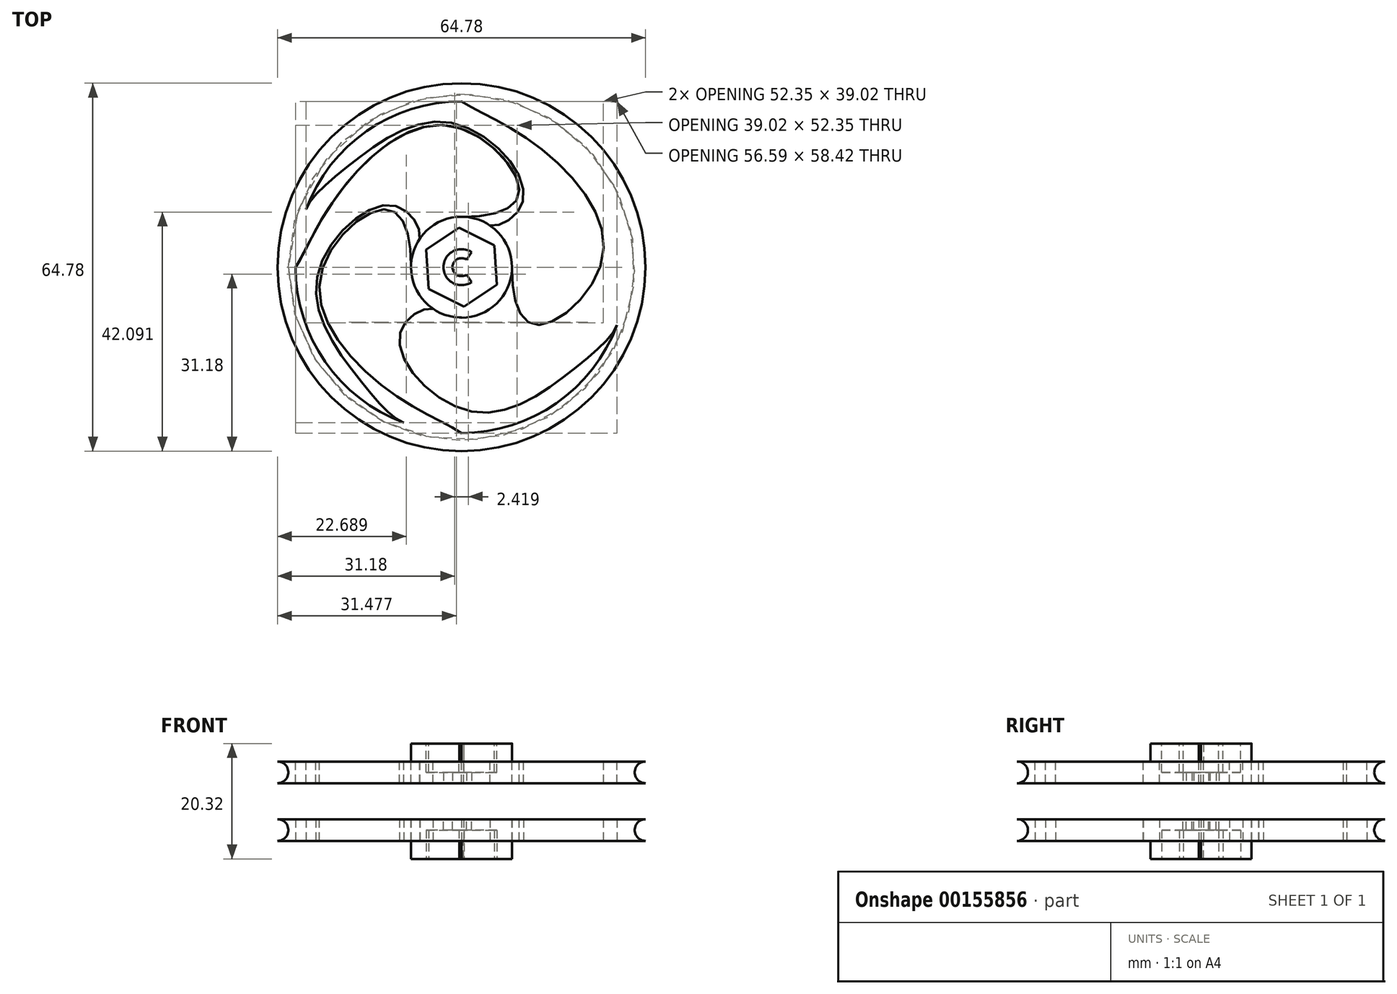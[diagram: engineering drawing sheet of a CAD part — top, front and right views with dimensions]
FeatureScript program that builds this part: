
annotation { "Feature Type Name" : "Feature", "Feature Type Description" : "" }
export const myFeature = defineFeature(function(context is Context, id is Id, definition is map)
    precondition{}
    {
        {
            var Q0;
            Q0=qCreatedBy(makeId("Front.planeOp"),FACE);
            var sketch = newSketch(context, id + "F0", { "sketchPlane" : qUnion([Q0])});
            skLineSegment(sketch, "E0.bottom", {"start": v(-32.39, 0) * mm, "end": v(0, 0) * mm, "construction": true});
            skLineSegment(sketch, "E0.top", {"start": v(-32.39, 1.9) * mm, "end": v(0, 1.9) * mm});
            skLineSegment(sketch, "E0.left", {"start": v(-32.39, 0) * mm, "end": v(-32.39, 1.9) * mm, "construction": true});
            skLineSegment(sketch, "E0.right", {"start": v(0, 0) * mm, "end": v(0, 1.9) * mm});
            skArc(sketch, "E1", {"start": v(-30.48, 0) * mm, "mid": v(-31.04, 1.35) * mm, "end": v(-32.39, 1.9) * mm});
            skArc(sketch, "E2.MirrorCS", {"start": v(-30.48, 0) * mm, "mid": v(-31.04, -1.35) * mm, "end": v(-32.39, -1.9) * mm});
            skLineSegment(sketch, "E3.MirrorCS", {"start": v(-32.39, -1.9) * mm, "end": v(0, -1.9) * mm});
            skLineSegment(sketch, "E4.MirrorCS", {"start": v(0, 0) * mm, "end": v(0, -1.9) * mm});
            skSolve(sketch);
        }
        {
            var Q0;
            Q0=qCreatedBy(makeId("Top.planeOp"),FACE);
            var sketch = newSketch(context, id + "F1", { "sketchPlane" : qUnion([Q0])});
            skCircle(sketch, "E5", {"center": v(0, 0) * mm, "radius": 30.48 * mm});
            skCircle(sketch, "E6", {"center": v(0, 0) * mm, "radius": 29.21 * mm});
            skCircle(sketch, "E7", {"center": v(0, 0) * mm, "radius": 8.9 * mm});
            skLineSegment(sketch, "E8", {"start": v(0, 0) * mm, "end": v(-39.84, 0) * mm, "construction": true});
            skLineSegment(sketch, "E9", {"start": v(0, 0) * mm, "end": v(0, -39.36) * mm, "construction": true});
            skFitSpline(sketch, "E10", {"points": [v(-8.9, 0) * mm, v(-12.79, 10.1) * mm, v(-24.86, -1.8) * mm, v(-12.95, -21.64) * mm, v(0, -29.21) * mm], "startDerivative": vector(1.91, 63.3) * mm, "endDerivative": vector(33.3, -21.4) * mm});
            skFitSpline(sketch, "E11", {"points": [v(-7.36, 4.99) * mm, v(-12.23, 10.9) * mm, v(-25.42, -1.73) * mm, v(-17.66, -20.12) * mm, v(-10.17, -27.38) * mm], "startDerivative": vector(6.17, 34.05) * mm, "endDerivative": vector(31.5, -11.78) * mm});
            skLineSegment(sketch, "E12", {"start": v(0, 0) * mm, "end": v(39.29, -39.29) * mm, "construction": true});
            skFitSpline(sketch, "E13.MirrorCS", {"points": [v(0, -8.9) * mm, v(-10.1, -12.79) * mm, v(1.8, -24.86) * mm, v(21.64, -12.95) * mm, v(29.21, 0) * mm], "startDerivative": vector(-63.3, 1.91) * mm, "endDerivative": vector(21.4, 33.3) * mm});
            skFitSpline(sketch, "E14.MirrorCS", {"points": [v(-4.99, -7.36) * mm, v(-10.9, -12.23) * mm, v(1.73, -25.42) * mm, v(20.12, -17.66) * mm, v(27.38, -10.17) * mm], "startDerivative": vector(-34.05, 6.17) * mm, "endDerivative": vector(11.78, 31.5) * mm});
            skFitSpline(sketch, "E15.MirrorCS", {"points": [v(7.36, -4.99) * mm, v(12.23, -10.9) * mm, v(25.42, 1.73) * mm, v(17.66, 20.12) * mm, v(10.17, 27.38) * mm], "startDerivative": vector(-6.17, -34.05) * mm, "endDerivative": vector(-31.5, 11.78) * mm});
            skFitSpline(sketch, "E16.MirrorCS", {"points": [v(8.9, 0) * mm, v(12.79, -10.1) * mm, v(24.86, 1.8) * mm, v(12.95, 21.64) * mm, v(0, 29.2) * mm], "startDerivative": vector(-1.91, -63.3) * mm, "endDerivative": vector(-33.3, 21.4) * mm});
            skFitSpline(sketch, "E17.MirrorCS", {"points": [v(8.9, 0) * mm, v(12.79, -10.1) * mm, v(24.86, 1.8) * mm, v(12.95, 21.64) * mm, v(0, 29.21) * mm], "startDerivative": vector(-1.91, -63.3) * mm, "endDerivative": vector(-33.3, 21.4) * mm});
            skFitSpline(sketch, "E18.MirrorCS", {"points": [v(7.36, -4.99) * mm, v(12.23, -10.9) * mm, v(25.42, 1.73) * mm, v(17.66, 20.12) * mm, v(10.17, 27.38) * mm], "startDerivative": vector(-6.17, -34.05) * mm, "endDerivative": vector(-31.5, 11.78) * mm});
            skFitSpline(sketch, "E19.MirrorCS", {"points": [v(4.99, 7.36) * mm, v(10.9, 12.23) * mm, v(-1.73, 25.42) * mm, v(-20.12, 17.66) * mm, v(-27.38, 10.17) * mm], "startDerivative": vector(34.05, -6.17) * mm, "endDerivative": vector(-11.78, -31.5) * mm});
            skFitSpline(sketch, "E20.MirrorCS", {"points": [v(0, 8.89) * mm, v(10.1, 12.79) * mm, v(-1.8, 24.86) * mm, v(-21.64, 12.95) * mm, v(-29.21, 0) * mm], "startDerivative": vector(63.3, -1.91) * mm, "endDerivative": vector(-21.4, -33.3) * mm});
            skSolve(sketch);
        }
        {
            var Q0;
            Q0=makeQuery(id+"F0.imprint","IMPRINT",FACE,{"disambiguationData":[TD([[makeQuery(id+"F0.imprint","IMPRINT",EDGE,{"derivedFrom":sQuery(id+"F0.wireOp",EDGE,"E0.top")}),-1.0]])]});
            var Q1;
            Q1=sQuery(id+"F0.wireOp",EDGE,"E0.right");
            revolve(context, id + "F2", {"entities" : qUnion([Q0]), "axis" : qUnion([Q1]), "revolveType" : RevolveType.FULL});
        }
        {
            var Q0;
            {var subQ6=sQuery(id+"F1.wireOp",EDGE,"E18.MirrorCS");Q0=makeQuery(id+"F1.imprint","IMPRINT",FACE,{"disambiguationData":[TD([[makeQuery(id+"F1.imprint","IMPRINT",EDGE,{"derivedFrom":subQ6}),-1.0]])]});}
            var Q1;
            {var subQ6=sQuery(id+"F1.wireOp",EDGE,"E14.MirrorCS");Q1=makeQuery(id+"F1.imprint","IMPRINT",FACE,{"disambiguationData":[TD([[makeQuery(id+"F1.imprint","IMPRINT",EDGE,{"derivedFrom":subQ6}),-1.0]])]});}
            var Q2;
            {var subQ0=sQuery(id+"F1.wireOp",EDGE,"E11");Q2=makeQuery(id+"F1.imprint","IMPRINT",FACE,{"disambiguationData":[TD([[makeQuery(id+"F1.imprint","IMPRINT",EDGE,{"derivedFrom":subQ0}),-1.0]])]});}
            var Q3;
            {var subQ6=sQuery(id+"F1.wireOp",EDGE,"E19.MirrorCS");Q3=makeQuery(id+"F1.imprint","IMPRINT",FACE,{"disambiguationData":[TD([[makeQuery(id+"F1.imprint","IMPRINT",EDGE,{"derivedFrom":subQ6}),-1.0]])]});}
            extrude(context, id + "F3", {"entities" : qUnion([Q0, Q1, Q2, Q3]), "operationType" : NewBodyOperationType.REMOVE, "oppositeDirection" : true, "depth" : 25.4 * mm, "symmetric" : true});
        }
        {
            var Q0;
            {var subQ0=sQuery(id+"F1.wireOp",EDGE,"E7");var subQ48=makeQuery(id+"F1.imprint","INTERSECT",VERTEX,{"derivedFrom":[subQ0,sQuery(id+"F1.wireOp",EDGE,"01417a5a-3fe0-4376-9868-93c7ef9975e0.4.36.0")]});Q0=makeQuery(id+"F1.imprint","IMPRINT",FACE,{"disambiguationData":[TD([[makeQuery(id+"F1.imprint","IMPRINT",EDGE,{"disambiguationData":[TD([[subQ48,-1.0]])],"derivedFrom":subQ0}),1.0]])]});}
            extrude(context, id + "F4", {"entities" : qUnion([Q0]), "operationType" : NewBodyOperationType.ADD, "depth" : 5.08 * mm});
        }
        {
            var Q0;
            Q0=makeQuery(id+"F4.opExtrude","CAP_FACE",FACE,{"disambiguationData":[OSD([sQuery(id+"F1.wireOp",EDGE,"E7")])],"isStart":false});
            var sketch = newSketch(context, id + "F5", { "sketchPlane" : qUnion([Q0])});
            skCircle(sketch, "E21.cCircle", {"center": v(0, 0) * mm, "radius": 6.03 * mm, "construction": true});
            skLineSegment(sketch, "E21.0", {"start": v(-0.43, 6.95) * mm, "end": v(5.8, 3.85) * mm});
            skLineSegment(sketch, "E21.1", {"start": v(5.8, 3.85) * mm, "end": v(6.24, -3.1) * mm});
            skLineSegment(sketch, "E21.2", {"start": v(6.24, -3.1) * mm, "end": v(0.43, -6.95) * mm});
            skLineSegment(sketch, "E21.3", {"start": v(0.43, -6.95) * mm, "end": v(-5.8, -3.85) * mm});
            skLineSegment(sketch, "E21.4", {"start": v(-5.8, -3.85) * mm, "end": v(-6.24, 3.1) * mm});
            skLineSegment(sketch, "E21.5", {"start": v(-6.24, 3.1) * mm, "end": v(-0.43, 6.95) * mm});
            skPoint(sketch, "E21.0.midPoint", {"position": v(2.69, 5.4) * mm});
            skSolve(sketch);
        }
        {
            var Q0;
            Q0=makeQuery(id+"F5.imprint","IMPRINT",FACE,{"disambiguationData":[TD([[makeQuery(id+"F5.imprint","IMPRINT",EDGE,{"derivedFrom":sQuery(id+"F5.wireOp",EDGE,"E21.0")}),-1.0]])]});
            extrude(context, id + "F6", {"entities" : qUnion([Q0]), "operationType" : NewBodyOperationType.REMOVE, "oppositeDirection" : true, "depth" : 5.08 * mm});
        }
        {
            var Q0;
            Q0=makeQuery(id+"F2.opRevolve","SWEPT_FACE",FACE,{"disambiguationData":[OSD([sQuery(id+"F0.wireOp",EDGE,"E3.MirrorCS")])]});
            var sketch = newSketch(context, id + "F7", { "sketchPlane" : qUnion([Q0])});
            skArc(sketch, "E22", {"start": v(1.75, 2.65) * mm, "mid": v(-3.18, 0) * mm, "end": v(1.75, -2.65) * mm});
            skArc(sketch, "E23", {"start": v(0.87, 1.33) * mm, "mid": v(-1.59, 0) * mm, "end": v(0.87, -1.33) * mm});
            skLineSegment(sketch, "E24", {"start": v(0.87, 1.33) * mm, "end": v(1.75, 2.65) * mm});
            skLineSegment(sketch, "E25", {"start": v(0, 0) * mm, "end": v(8.16, 0) * mm, "construction": true});
            skLineSegment(sketch, "E26.MirrorCS", {"start": v(0.87, -1.33) * mm, "end": v(1.75, -2.65) * mm});
            skSolve(sketch);
        }
        {
            var Q0;
            Q0=makeQuery(id+"F7.imprint","IMPRINT",FACE,{"disambiguationData":[TD([[makeQuery(id+"F7.imprint","IMPRINT",EDGE,{"derivedFrom":sQuery(id+"F7.wireOp",EDGE,"E22")}),1.0]])]});
            extrude(context, id + "F8", {"entities" : qUnion([Q0]), "operationType" : NewBodyOperationType.REMOVE, "oppositeDirection" : true, "depth" : 12.7 * mm});
        }
        {
            var Q0;
            Q0=qCreatedBy(makeId("Top.planeOp"),FACE);
            cPlane(context, id + "F9", {"entities" : qUnion([Q0]), "cplaneType" : CPlaneType.OFFSET, "offset" : 5.08 * mm, "oppositeDirection" : true, "width" : 152.4 * mm, "height" : 152.4 * mm});
        }
        {
            var Q0;
            Q0=makeQuery(id+"F2.opRevolve","SWEPT_BODY",BODY,{"disambiguationData":[OSD([sQuery(id+"F0.wireOp",EDGE,"E0.top"),sQuery(id+"F0.wireOp",EDGE,"E0.right"),sQuery(id+"F0.wireOp",EDGE,"E1"),sQuery(id+"F0.wireOp",EDGE,"E2.MirrorCS"),sQuery(id+"F0.wireOp",EDGE,"E3.MirrorCS"),sQuery(id+"F0.wireOp",EDGE,"E4.MirrorCS")])]});
            var Q1;
            Q1=qCreatedBy(id+"F9.planeOp",FACE);
            mirror(context, id + "F10", {"entities" : qUnion([Q0]), "mirrorPlane" : qUnion([Q1])});
        }
    });
